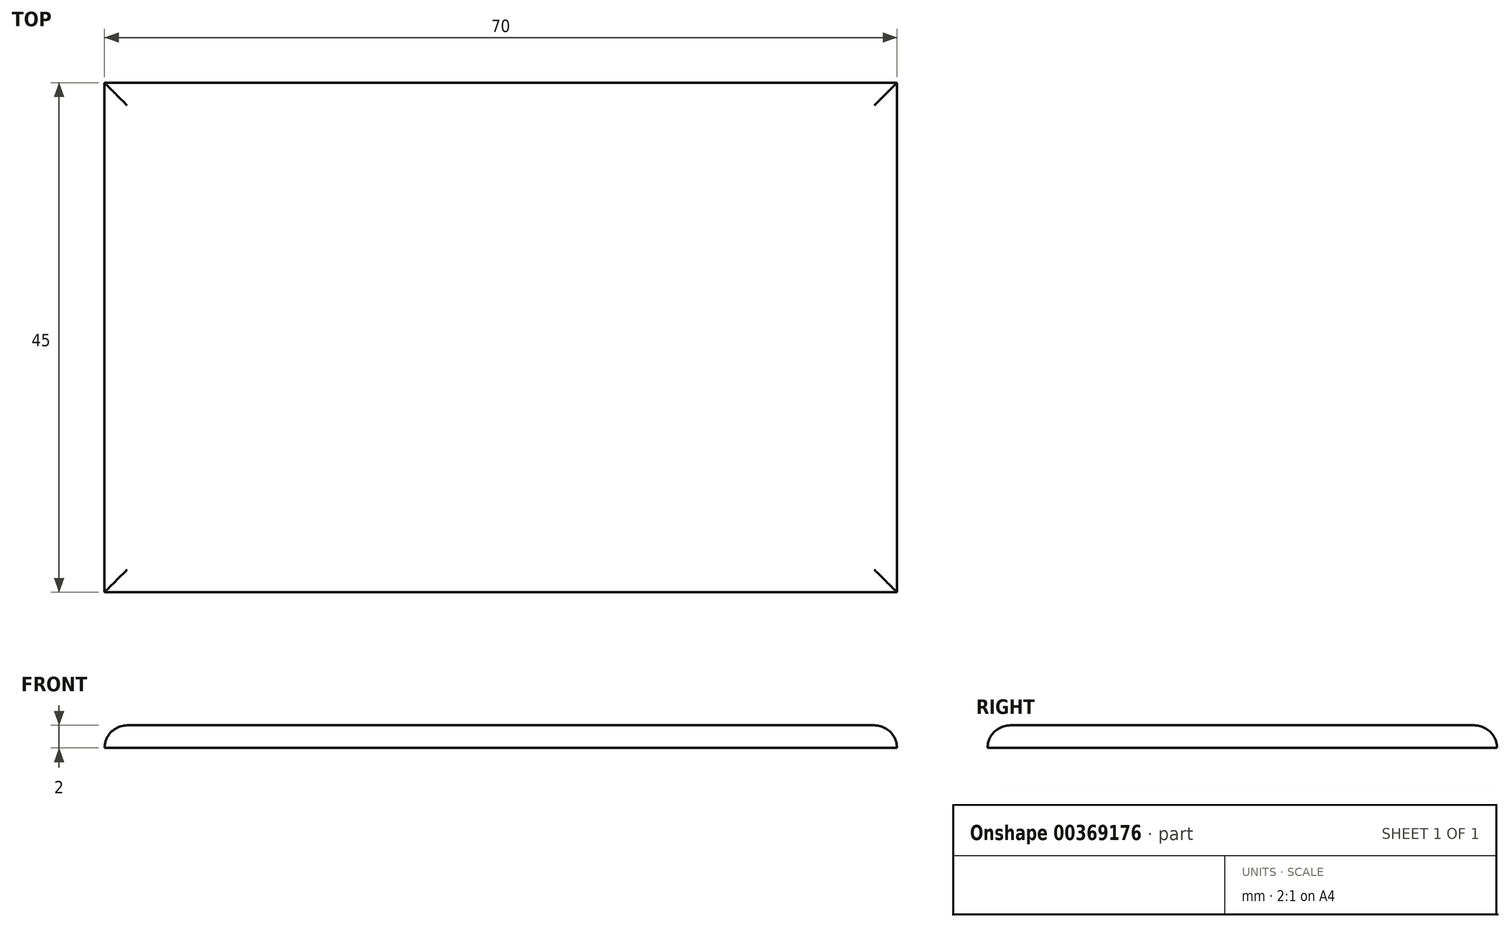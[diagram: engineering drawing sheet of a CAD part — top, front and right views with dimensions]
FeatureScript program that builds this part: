
annotation { "Feature Type Name" : "Feature", "Feature Type Description" : "" }
export const myFeature = defineFeature(function(context is Context, id is Id, definition is map)
    precondition{}
    {
        {
            var Q0;
            Q0=qCreatedBy(makeId("Top.planeOp"),FACE);
            var sketch = newSketch(context, id + "F0", { "sketchPlane" : qUnion([Q0])});
            skLineSegment(sketch, "E0.bottom", {"start": v(-64.48, 45) * mm, "end": v(5.52, 45) * mm});
            skLineSegment(sketch, "E0.top", {"start": v(-64.48, 0) * mm, "end": v(5.52, 0) * mm});
            skLineSegment(sketch, "E0.left", {"start": v(-64.48, 45) * mm, "end": v(-64.48, 0) * mm});
            skLineSegment(sketch, "E0.right", {"start": v(5.52, 45) * mm, "end": v(5.52, 0) * mm});
            skSolve(sketch);
        }
        {
            var Q0;
            Q0 = qSketchRegion(id + "F0", true);
            extrude(context, id + "F1", {"entities" : qUnion([Q0]), "depth" : 2 * mm});
        }
        {
            var Q0;
            Q0=makeQuery(id+"F1.opExtrude","CAP_EDGE",EDGE,{"disambiguationData":[OSD([sQuery(id+"F0.wireOp",EDGE,"E0.right")])],"isStart":false});
            var Q1;
            Q1=makeQuery(id+"F1.opExtrude","CAP_EDGE",EDGE,{"disambiguationData":[OSD([sQuery(id+"F0.wireOp",EDGE,"E0.top")])],"isStart":false});
            var Q2;
            Q2=makeQuery(id+"F1.opExtrude","CAP_EDGE",EDGE,{"disambiguationData":[OSD([sQuery(id+"F0.wireOp",EDGE,"E0.left")])],"isStart":false});
            var Q3;
            Q3=makeQuery(id+"F1.opExtrude","CAP_EDGE",EDGE,{"disambiguationData":[OSD([sQuery(id+"F0.wireOp",EDGE,"E0.bottom")])],"isStart":false});
            fillet(context, id + "F2", {"entities" : qUnion([Q0, Q1, Q2, Q3]), "radius" : 2 * mm, "tangentPropagation" : true, "allowEdgeOverflow" : false});
        }
    });
